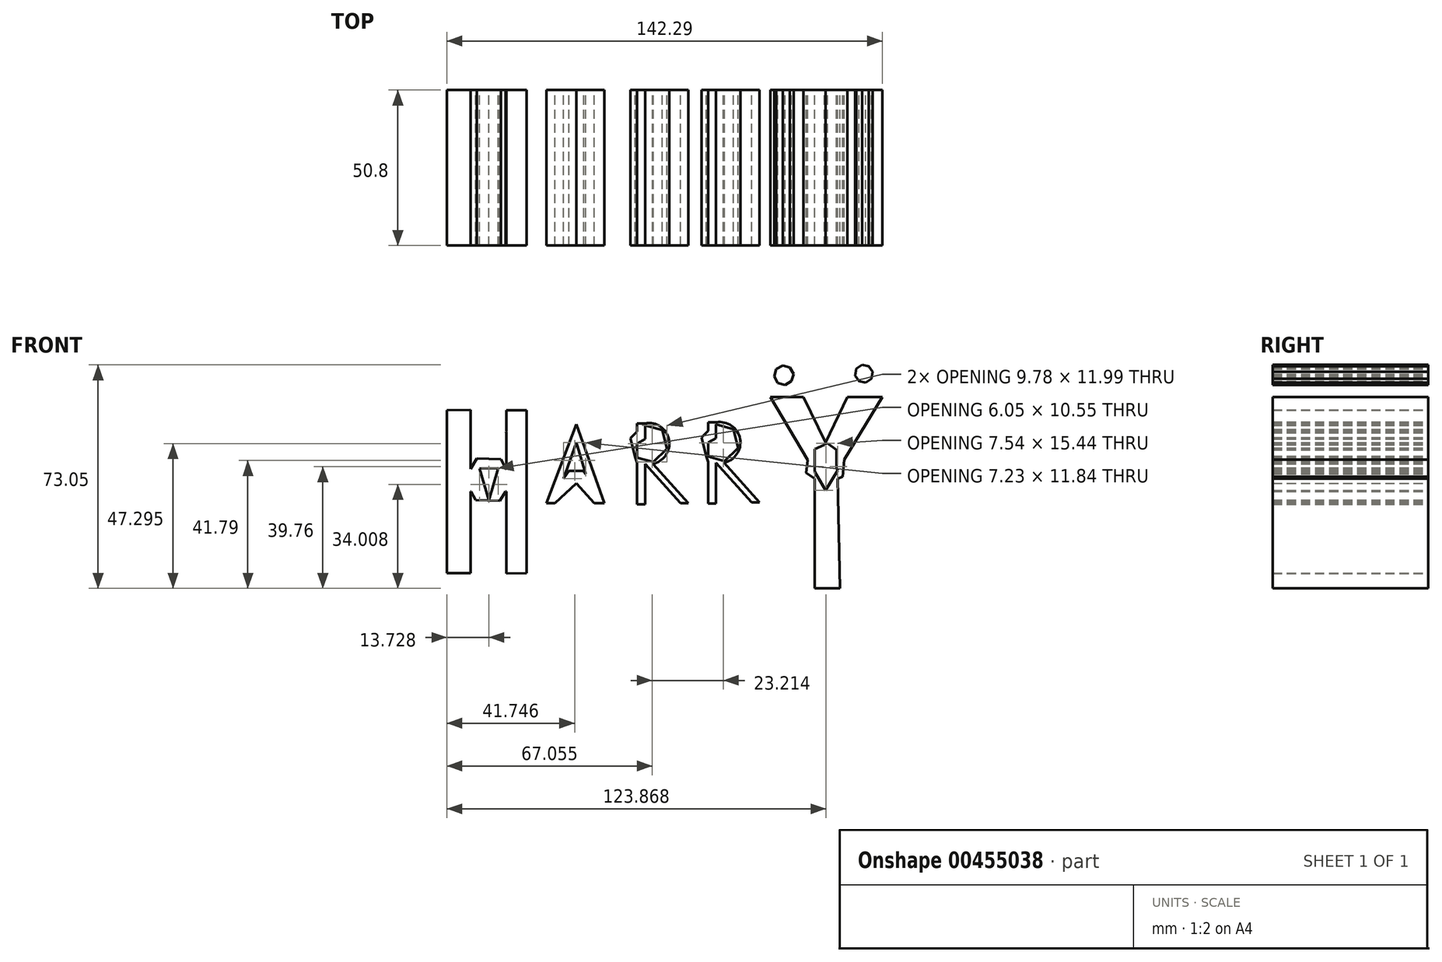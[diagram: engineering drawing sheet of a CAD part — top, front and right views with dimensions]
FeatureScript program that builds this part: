
annotation { "Feature Type Name" : "Feature", "Feature Type Description" : "" }
export const myFeature = defineFeature(function(context is Context, id is Id, definition is map)
    precondition{}
    {
        {
            var Q0;
            Q0=qCreatedBy(makeId("Front.planeOp"),FACE);
            var sketch = newSketch(context, id + "F0", { "sketchPlane" : qUnion([Q0])});
            skLineSegment(sketch, "E0", {"start": v(-66.55, 37.32) * mm, "end": v(-66.55, -15.84) * mm});
            skLineSegment(sketch, "E1", {"start": v(-66.55, -15.84) * mm, "end": v(-58.83, -15.84) * mm});
            skLineSegment(sketch, "E2", {"start": v(-58.83, -15.84) * mm, "end": v(-58.83, 37.5) * mm});
            skLineSegment(sketch, "E3", {"start": v(-58.83, 37.5) * mm, "end": v(-66.55, 37.32) * mm});
            skLineSegment(sketch, "E4", {"start": v(-58.83, 18.19) * mm, "end": v(-47.23, 18.46) * mm});
            skLineSegment(sketch, "E5", {"start": v(-47.23, 18.46) * mm, "end": v(-47.05, 10.83) * mm});
            skPoint(sketch, "E5.endSnap0", {"position": v(-58.83, 10.83) * mm});
            skLineSegment(sketch, "E6", {"start": v(-47.05, 10.83) * mm, "end": v(-58.83, 10.83) * mm});
            skLineSegment(sketch, "E7", {"start": v(-47.05, 37.32) * mm, "end": v(-47.05, -16.02) * mm});
            skLineSegment(sketch, "E8", {"start": v(-47.05, -16.02) * mm, "end": v(-40.46, -15.87) * mm});
            skLineSegment(sketch, "E9", {"start": v(-40.46, -15.87) * mm, "end": v(-40.46, 37.32) * mm});
            skLineSegment(sketch, "E10", {"start": v(-40.46, 37.32) * mm, "end": v(-47.05, 37.32) * mm});
            skCircle(sketch, "E11.cCircle", {"center": v(-53.03, 14.65) * mm, "radius": 6.8 * mm, "construction": true});
            skPoint(sketch, "E11.cCircle.centerSnap0", {"position": v(-53.03, 18.33) * mm});
            skPoint(sketch, "E11.cCircle.centerSnap1", {"position": v(-47.14, 14.65) * mm});
            skLineSegment(sketch, "E11.0", {"start": v(-60.87, 14.84) * mm, "end": v(-56.79, 21.54) * mm});
            skLineSegment(sketch, "E11.1", {"start": v(-56.79, 21.54) * mm, "end": v(-48.94, 21.34) * mm});
            skLineSegment(sketch, "E11.2", {"start": v(-48.94, 21.34) * mm, "end": v(-45.19, 14.45) * mm});
            skLineSegment(sketch, "E11.3", {"start": v(-45.19, 14.45) * mm, "end": v(-49.28, 7.76) * mm});
            skLineSegment(sketch, "E11.4", {"start": v(-49.28, 7.76) * mm, "end": v(-57.12, 7.95) * mm});
            skLineSegment(sketch, "E11.5", {"start": v(-57.12, 7.95) * mm, "end": v(-60.87, 14.84) * mm});
            skPoint(sketch, "E11.0.midPoint", {"position": v(-58.83, 18.19) * mm});
            skLineSegment(sketch, "E12", {"start": v(-56.79, 21.54) * mm, "end": v(-52.86, 7.85) * mm});
            skPoint(sketch, "E12.endSnap0", {"position": v(-53.2, 7.85) * mm});
            skLineSegment(sketch, "E13", {"start": v(-52.86, 7.85) * mm, "end": v(-48.94, 21.34) * mm});
            skLineSegment(sketch, "E14", {"start": v(-66.55, 37.32) * mm, "end": v(-58.83, 29.79) * mm});
            skLineSegment(sketch, "E15", {"start": v(-58.83, 29.79) * mm, "end": v(-66.55, 18.46) * mm});
            skLineSegment(sketch, "E16", {"start": v(-66.55, 18.46) * mm, "end": v(-58.83, 10.83) * mm});
            skLineSegment(sketch, "E17", {"start": v(-58.83, 10.83) * mm, "end": v(-66.55, 3.01) * mm});
            skLineSegment(sketch, "E18", {"start": v(-66.55, 3.01) * mm, "end": v(-58.83, -6.28) * mm});
            skLineSegment(sketch, "E19", {"start": v(-58.83, -6.28) * mm, "end": v(-66.55, -15.84) * mm});
            skLineSegment(sketch, "E20", {"start": v(-40.46, 37.32) * mm, "end": v(-47.23, 30.35) * mm});
            skLineSegment(sketch, "E21", {"start": v(-47.23, 30.35) * mm, "end": v(-40.46, 18.46) * mm});
            skLineSegment(sketch, "E22", {"start": v(-40.46, 18.46) * mm, "end": v(-47.05, 10.83) * mm});
            skLineSegment(sketch, "E23", {"start": v(-47.05, 10.83) * mm, "end": v(-40.46, 5.14) * mm});
            skLineSegment(sketch, "E24", {"start": v(-40.46, 5.14) * mm, "end": v(-47.05, -5.72) * mm});
            skLineSegment(sketch, "E25", {"start": v(-47.05, -5.72) * mm, "end": v(-40.46, -15.87) * mm});
            skLineSegment(sketch, "E26", {"start": v(-24.25, 32.72) * mm, "end": v(-34, 6.97) * mm});
            skLineSegment(sketch, "E27", {"start": v(-34, 6.97) * mm, "end": v(-31.24, 6.97) * mm});
            skLineSegment(sketch, "E28", {"start": v(-31.24, 6.97) * mm, "end": v(-24.25, 26.83) * mm});
            skLineSegment(sketch, "E29", {"start": v(-24.25, 26.83) * mm, "end": v(-18.37, 6.97) * mm});
            skLineSegment(sketch, "E30", {"start": v(-18.37, 6.97) * mm, "end": v(-15.06, 6.97) * mm});
            skLineSegment(sketch, "E31", {"start": v(-15.06, 6.97) * mm, "end": v(-24.25, 32.72) * mm});
            skCircle(sketch, "E32.cCircle", {"center": v(-24.25, 16.16) * mm, "radius": 2.76 * mm, "construction": true});
            skLineSegment(sketch, "E32.0", {"start": v(-24.25, 13.4) * mm, "end": v(-26.64, 17.54) * mm});
            skLineSegment(sketch, "E32.1", {"start": v(-26.64, 17.54) * mm, "end": v(-21.86, 17.54) * mm});
            skLineSegment(sketch, "E32.2", {"start": v(-21.86, 17.54) * mm, "end": v(-24.25, 13.4) * mm});
            skLineSegment(sketch, "E33", {"start": v(-26.64, 17.54) * mm, "end": v(-27.4, 24.38) * mm});
            skLineSegment(sketch, "E34", {"start": v(-27.4, 24.38) * mm, "end": v(-24.25, 26.83) * mm});
            skLineSegment(sketch, "E35", {"start": v(-24.25, 26.83) * mm, "end": v(-21.28, 24.39) * mm});
            skLineSegment(sketch, "E36", {"start": v(-21.28, 24.39) * mm, "end": v(-21.86, 17.54) * mm});
            skLineSegment(sketch, "E37", {"start": v(-26.64, 17.54) * mm, "end": v(-34, 6.97) * mm});
            skLineSegment(sketch, "E38", {"start": v(-21.86, 17.54) * mm, "end": v(-15.06, 6.97) * mm});
            skLineSegment(sketch, "E39", {"start": v(-24.25, 26.83) * mm, "end": v(-24.25, 32.72) * mm});
            skLineSegment(sketch, "E40", {"start": v(-24.25, 13.4) * mm, "end": v(-31.24, 6.97) * mm});
            skLineSegment(sketch, "E41", {"start": v(-24.25, 13.4) * mm, "end": v(-18.37, 6.97) * mm});
            skLineSegment(sketch, "E42", {"start": v(-4.39, 33.09) * mm, "end": v(-4.39, 6.6) * mm});
            skLineSegment(sketch, "E43", {"start": v(-4.39, 6.6) * mm, "end": v(-1.81, 6.6) * mm});
            skLineSegment(sketch, "E44", {"start": v(-1.81, 6.6) * mm, "end": v(-1.81, 33.09) * mm});
            skLineSegment(sketch, "E45", {"start": v(-4.39, 33.09) * mm, "end": v(-1.81, 33.09) * mm});
            skArc(sketch, "E46", {"start": v(-1.81, 19.84) * mm, "mid": v(6.12, 26.46) * mm, "end": v(-1.81, 33.09) * mm});
            skLineSegment(sketch, "E47", {"start": v(-1.81, 19.84) * mm, "end": v(9.78, 6.97) * mm});
            skLineSegment(sketch, "E48", {"start": v(9.78, 6.97) * mm, "end": v(12.35, 6.97) * mm});
            skLineSegment(sketch, "E49", {"start": v(12.35, 6.97) * mm, "end": v(0.76, 19.84) * mm});
            skLineSegment(sketch, "E50", {"start": v(0.76, 19.84) * mm, "end": v(-1.81, 19.84) * mm});
            skCircle(sketch, "E51.cCircle", {"center": v(-0.61, 26.46) * mm, "radius": 5.4 * mm, "construction": true});
            skLineSegment(sketch, "E51.0", {"start": v(-6.62, 28.15) * mm, "end": v(-2.16, 32.5) * mm});
            skLineSegment(sketch, "E51.1", {"start": v(-2.16, 32.5) * mm, "end": v(3.85, 30.83) * mm});
            skLineSegment(sketch, "E51.2", {"start": v(3.85, 30.83) * mm, "end": v(5.4, 24.78) * mm});
            skLineSegment(sketch, "E51.3", {"start": v(5.4, 24.78) * mm, "end": v(0.94, 20.42) * mm});
            skLineSegment(sketch, "E51.4", {"start": v(0.94, 20.42) * mm, "end": v(-5.07, 22.1) * mm});
            skLineSegment(sketch, "E51.5", {"start": v(-5.07, 22.1) * mm, "end": v(-6.62, 28.15) * mm});
            skPoint(sketch, "E51.0.midPoint", {"position": v(-4.39, 30.33) * mm});
            skCircle(sketch, "E52.cCircle", {"center": v(-0.61, 26.46) * mm, "radius": 3.78 * mm, "construction": true});
            skLineSegment(sketch, "E52.0", {"start": v(-4.39, 26.46) * mm, "end": v(1.28, 29.73) * mm});
            skLineSegment(sketch, "E52.1", {"start": v(1.28, 29.73) * mm, "end": v(1.28, 23.2) * mm});
            skLineSegment(sketch, "E52.2", {"start": v(1.28, 23.2) * mm, "end": v(-4.39, 26.46) * mm});
            skLineSegment(sketch, "E53", {"start": v(-5.07, 22.1) * mm, "end": v(-1.81, 12.98) * mm});
            skLineSegment(sketch, "E54", {"start": v(-1.81, 12.98) * mm, "end": v(-4.39, 6.6) * mm});
            skLineSegment(sketch, "E55", {"start": v(12.35, 6.97) * mm, "end": v(6.05, 11.1) * mm});
            skLineSegment(sketch, "E56", {"start": v(6.05, 11.1) * mm, "end": v(4.36, 15.85) * mm});
            skLineSegment(sketch, "E57", {"start": v(4.36, 15.85) * mm, "end": v(-1.81, 19.84) * mm});
            skLineSegment(sketch, "E58", {"start": v(18.83, 33.39) * mm, "end": v(18.83, 6.9) * mm});
            skLineSegment(sketch, "E59", {"start": v(18.83, 6.9) * mm, "end": v(21.4, 6.9) * mm});
            skLineSegment(sketch, "E60", {"start": v(21.4, 6.9) * mm, "end": v(21.4, 33.39) * mm});
            skLineSegment(sketch, "E61", {"start": v(18.83, 33.39) * mm, "end": v(21.4, 33.39) * mm});
            skArc(sketch, "E62", {"start": v(21.4, 20.15) * mm, "mid": v(29.33, 26.77) * mm, "end": v(21.4, 33.39) * mm});
            skLineSegment(sketch, "E63", {"start": v(21.4, 20.15) * mm, "end": v(32.99, 7.27) * mm});
            skLineSegment(sketch, "E64", {"start": v(32.99, 7.27) * mm, "end": v(35.56, 7.27) * mm});
            skLineSegment(sketch, "E65", {"start": v(35.56, 7.27) * mm, "end": v(23.98, 20.15) * mm});
            skLineSegment(sketch, "E66", {"start": v(23.98, 20.15) * mm, "end": v(21.4, 20.15) * mm});
            skCircle(sketch, "E67.cCircle", {"center": v(22.6, 26.77) * mm, "radius": 5.4 * mm, "construction": true});
            skLineSegment(sketch, "E67.0", {"start": v(16.6, 28.45) * mm, "end": v(21.06, 32.81) * mm});
            skLineSegment(sketch, "E67.1", {"start": v(21.06, 32.81) * mm, "end": v(27.06, 31.13) * mm});
            skLineSegment(sketch, "E67.2", {"start": v(27.06, 31.13) * mm, "end": v(28.61, 25.09) * mm});
            skLineSegment(sketch, "E67.3", {"start": v(28.61, 25.09) * mm, "end": v(24.15, 20.72) * mm});
            skLineSegment(sketch, "E67.4", {"start": v(24.15, 20.72) * mm, "end": v(18.14, 22.4) * mm});
            skLineSegment(sketch, "E67.5", {"start": v(18.14, 22.4) * mm, "end": v(16.6, 28.45) * mm});
            skPoint(sketch, "E67.0.midPoint", {"position": v(18.83, 30.63) * mm});
            skCircle(sketch, "E68.cCircle", {"center": v(22.6, 26.77) * mm, "radius": 3.78 * mm, "construction": true});
            skLineSegment(sketch, "E68.0", {"start": v(18.83, 26.77) * mm, "end": v(24.5, 30.04) * mm});
            skLineSegment(sketch, "E68.1", {"start": v(24.5, 30.04) * mm, "end": v(24.5, 23.5) * mm});
            skLineSegment(sketch, "E68.2", {"start": v(24.5, 23.5) * mm, "end": v(18.83, 26.77) * mm});
            skLineSegment(sketch, "E69", {"start": v(18.14, 22.4) * mm, "end": v(21.4, 13.28) * mm});
            skLineSegment(sketch, "E70", {"start": v(21.4, 13.28) * mm, "end": v(18.83, 6.9) * mm});
            skLineSegment(sketch, "E71", {"start": v(35.56, 7.27) * mm, "end": v(29.27, 11.4) * mm});
            skLineSegment(sketch, "E72", {"start": v(29.27, 11.4) * mm, "end": v(27.57, 16.15) * mm});
            skLineSegment(sketch, "E73", {"start": v(27.57, 16.15) * mm, "end": v(21.4, 20.15) * mm});
            skLineSegment(sketch, "E74", {"start": v(39.18, 41.63) * mm, "end": v(49.98, 41.63) * mm});
            skLineSegment(sketch, "E75", {"start": v(49.98, 41.63) * mm, "end": v(57.12, 26.83) * mm});
            skLineSegment(sketch, "E76", {"start": v(57.12, 26.83) * mm, "end": v(64.25, 41.63) * mm});
            skLineSegment(sketch, "E77", {"start": v(64.25, 41.63) * mm, "end": v(75.74, 41.63) * mm});
            skLineSegment(sketch, "E78", {"start": v(39.18, 41.63) * mm, "end": v(57.12, 11.16) * mm});
            skLineSegment(sketch, "E79", {"start": v(57.12, 11.16) * mm, "end": v(75.74, 41.63) * mm});
            skLineSegment(sketch, "E80", {"start": v(53.55, 17.22) * mm, "end": v(53.55, -20.88) * mm});
            skPoint(sketch, "E80.startSnap0", {"position": v(53.55, 34.23) * mm});
            skLineSegment(sketch, "E81", {"start": v(53.55, -20.88) * mm, "end": v(61.82, -20.88) * mm});
            skLineSegment(sketch, "E82", {"start": v(61.82, -20.88) * mm, "end": v(61.09, 17.66) * mm});
            skLineSegment(sketch, "E83", {"start": v(61.09, 17.66) * mm, "end": v(57.12, 26.83) * mm});
            skLineSegment(sketch, "E84", {"start": v(53.55, 17.22) * mm, "end": v(57.12, 26.83) * mm});
            skLineSegment(sketch, "E85", {"start": v(60.68, 34.23) * mm, "end": v(75.74, 41.63) * mm});
            skLineSegment(sketch, "E86", {"start": v(60.68, 34.23) * mm, "end": v(60.68, 18.6) * mm});
            skLineSegment(sketch, "E87", {"start": v(60.68, 18.6) * mm, "end": v(53.55, 34.23) * mm});
            skLineSegment(sketch, "E88", {"start": v(53.55, 34.23) * mm, "end": v(53.55, 17.22) * mm});
            skLineSegment(sketch, "E89", {"start": v(53.55, 34.23) * mm, "end": v(39.18, 41.63) * mm});
            skLineSegment(sketch, "E90", {"start": v(57.12, 11.16) * mm, "end": v(53.55, -20.88) * mm});
            skLineSegment(sketch, "E91", {"start": v(57.46, 10.29) * mm, "end": v(57.12, 11.16) * mm});
            skLineSegment(sketch, "E92", {"start": v(57.46, 10.29) * mm, "end": v(61.82, -20.88) * mm});
            skLineSegment(sketch, "E93", {"start": v(53.55, 17.22) * mm, "end": v(61.09, 17.66) * mm});
            skLineSegment(sketch, "E94", {"start": v(60.68, 34.23) * mm, "end": v(71.22, 34.23) * mm});
            skLineSegment(sketch, "E95", {"start": v(71.22, 34.23) * mm, "end": v(61.09, 17.66) * mm});
            skLineSegment(sketch, "E96", {"start": v(53.55, 34.23) * mm, "end": v(43.54, 34.23) * mm});
            skCircle(sketch, "E97.cCircle", {"center": v(57.12, 19.7) * mm, "radius": 6.86 * mm, "construction": true});
            skLineSegment(sketch, "E97.0", {"start": v(51.54, 23.7) * mm, "end": v(57.8, 26.52) * mm});
            skLineSegment(sketch, "E97.1", {"start": v(57.8, 26.52) * mm, "end": v(63.37, 22.51) * mm});
            skLineSegment(sketch, "E97.2", {"start": v(63.37, 22.51) * mm, "end": v(62.69, 15.69) * mm});
            skLineSegment(sketch, "E97.3", {"start": v(62.69, 15.69) * mm, "end": v(56.43, 12.86) * mm});
            skLineSegment(sketch, "E97.4", {"start": v(56.43, 12.86) * mm, "end": v(50.86, 16.87) * mm});
            skLineSegment(sketch, "E97.5", {"start": v(50.86, 16.87) * mm, "end": v(51.54, 23.7) * mm});
            skCircle(sketch, "E98.cCircle", {"center": v(43.54, 48.78) * mm, "radius": 3.19 * mm, "construction": true});
            skLineSegment(sketch, "E98.0", {"start": v(46.04, 46.81) * mm, "end": v(43.92, 45.61) * mm});
            skLineSegment(sketch, "E98.1", {"start": v(43.92, 45.61) * mm, "end": v(41.57, 46.27) * mm});
            skLineSegment(sketch, "E98.2", {"start": v(41.57, 46.27) * mm, "end": v(40.37, 48.4) * mm});
            skLineSegment(sketch, "E98.3", {"start": v(40.37, 48.4) * mm, "end": v(41.03, 50.75) * mm});
            skLineSegment(sketch, "E98.4", {"start": v(41.03, 50.75) * mm, "end": v(43.16, 51.94) * mm});
            skLineSegment(sketch, "E98.5", {"start": v(43.16, 51.94) * mm, "end": v(45.5, 51.29) * mm});
            skLineSegment(sketch, "E98.6", {"start": v(45.5, 51.29) * mm, "end": v(46.7, 49.16) * mm});
            skLineSegment(sketch, "E98.7", {"start": v(46.7, 49.16) * mm, "end": v(46.04, 46.81) * mm});
            skCircle(sketch, "E99.cCircle", {"center": v(69.67, 49.27) * mm, "radius": 2.96 * mm, "construction": true});
            skLineSegment(sketch, "E99.0", {"start": v(72.14, 47.63) * mm, "end": v(70.25, 46.37) * mm});
            skLineSegment(sketch, "E99.1", {"start": v(70.25, 46.37) * mm, "end": v(68.03, 46.81) * mm});
            skLineSegment(sketch, "E99.2", {"start": v(68.03, 46.81) * mm, "end": v(66.77, 48.7) * mm});
            skLineSegment(sketch, "E99.3", {"start": v(66.77, 48.7) * mm, "end": v(67.21, 50.91) * mm});
            skLineSegment(sketch, "E99.4", {"start": v(67.21, 50.91) * mm, "end": v(69.1, 52.17) * mm});
            skLineSegment(sketch, "E99.5", {"start": v(69.1, 52.17) * mm, "end": v(71.32, 51.73) * mm});
            skLineSegment(sketch, "E99.6", {"start": v(71.32, 51.73) * mm, "end": v(72.58, 49.85) * mm});
            skLineSegment(sketch, "E99.7", {"start": v(72.58, 49.85) * mm, "end": v(72.14, 47.63) * mm});
            skSolve(sketch);
        }
        {
            var Q0;
            Q0 = qSketchRegion(id + "F0", true);
            extrude(context, id + "F1", {"entities" : qUnion([Q0]), "depth" : 50.8 * mm});
        }
    });
